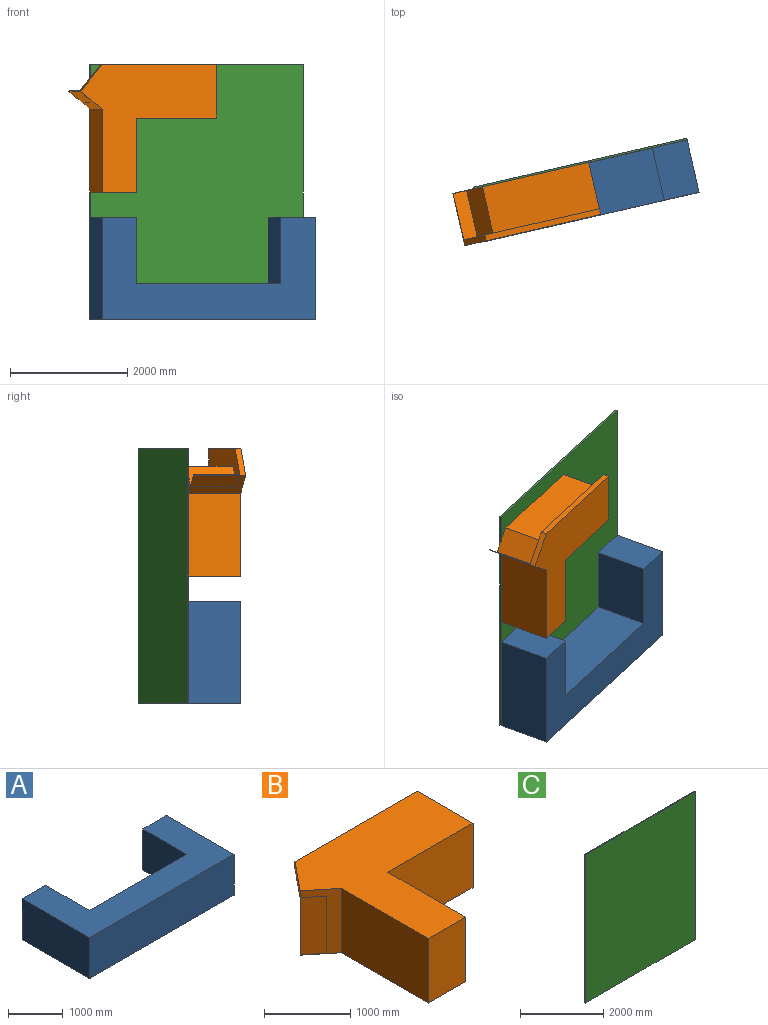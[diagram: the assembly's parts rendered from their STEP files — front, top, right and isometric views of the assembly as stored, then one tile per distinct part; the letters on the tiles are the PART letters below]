
ASSEMBLY  parts=3 mates=2
PART A: 10 faces, bbox 3733.8x1746.3x914.4 mm
  f0: plane 914.4x609.6mm, normal (0,1,0), area 557418.2mm2, adj f3,f5,f6,f7
  f1: plane 1746.25x914.4mm, normal (1,0,0), area 1596771mm2, adj f2,f4,f5,f6
  f2: plane 914.4x609.6mm, normal (0,1,0), area 557418.2mm2, adj f1,f5,f6,f9
  f3: plane 1746.25x914.4mm, normal (-1,0,0), area 1596771mm2, adj f0,f4,f5,f6
  f4: plane 3733.8x914.4mm, normal (0,-1,0), area 3414186.7mm2, adj f1,f3,f5,f6
  f5: plane 3733.8x1746.25mm, normal (0,0,1), area 3661928.2mm2, adj f0,f1,f2,f3,f4,f7,f8,f9
  f6: plane 3733.8x1746.25mm, normal (0,0,-1), area 3661928.2mm2, adj f0,f1,f2,f3,f4,f7,f8,f9
  f7: plane 1136.65x914.4mm, normal (1,0,0), area 1039352.8mm2, adj f0,f5,f6,f8
  f8: plane 2514.6x914.4mm, normal (0,1,0), area 2299350.2mm2, adj f5,f6,f7,f9
  f9: plane 1136.65x914.4mm, normal (-1,0,0), area 1039352.8mm2, adj f2,f5,f6,f8
PART B: 14 faces, bbox 2379.9x2190.2x914.4 mm
  f0: plane 2379.9x1885.4mm, normal (0,0,-1), area 2009196.6mm2, adj f1,f2,f4,f5,f6,f7,f8,f9
  f1: plane 1861.97x812.8mm, normal (0,1,0), area 1513411.7mm2, adj f0,f2,f11,f13
  f2: plane 914.4x914.4mm, normal (1,0,0), area 588385.9mm2, adj f0,f1,f3,f5,f10,f11
  f3: plane 2006.6x101.6mm, normal (0,1,0), area 203870.6mm2, adj f2,f6,f10,f11
  f4: plane 1275.8x914.4mm, normal (1,0,0), area 1166590.4mm2, adj f0,f5,f9,f10
  f5: plane 1397x914.4mm, normal (0,-1,0), area 1277416.8mm2, adj f0,f2,f4,f10
  f6: plane 914.4x457.2mm, normal (-0.77,0.63,0), area 64880.1mm2, adj f0,f3,f7,f10,f11,f12
  f7: plane 914.4x373.3mm, normal (-0.63,-0.77,0), area 440677.8mm2, adj f0,f6,f8,f10
  f8: plane 1428.2x914.4mm, normal (-1,0,0), area 1305945mm2, adj f0,f7,f9,f10
  f9: plane 914.4x609.6mm, normal (0,-1,0), area 557418.2mm2, adj f0,f4,f8,f10
  f10: plane 2379.9x2190.2mm, normal (0,0,1), area 2754790.2mm2, adj f2,f3,f4,f5,f6,f7,f8,f9
  f11: plane 2376.08x645.29mm, normal (0,0,-1), area 745593.5mm2, adj f1,f2,f3,f6,f12,f13
  f12: plane 812.8x236.1mm, normal (0.63,0.77,0), area 247741.4mm2, adj f0,f6,f11,f13
  f13: plane 812.8x340.49mm, normal (-0.77,0.63,0), area 357285mm2, adj f0,f1,f11,f12
PART C: 6 faces, bbox 3733.8x25.4x4356.1 mm
  f0: plane 4356.1x25.4mm, normal (1,0,0), area 110644.9mm2, adj f1,f3,f4,f5
  f1: plane 3733.8x25.4mm, normal (0,0,1), area 94838.5mm2, adj f0,f2,f4,f5
  f2: plane 4356.1x25.4mm, normal (-1,0,0), area 110644.9mm2, adj f1,f3,f4,f5
  f3: plane 3733.8x25.4mm, normal (0,0,-1), area 94838.5mm2, adj f0,f2,f4,f5
  f4: plane 4356.1x3733.8mm, normal (0,-1,0), area 16264806.2mm2, adj f0,f1,f2,f3
  f5: plane 4356.1x3733.8mm, normal (0,1,0), area 16264806.2mm2, adj f0,f1,f2,f3
PLACE A rot(axis=(0.99,0.11,0.11),90.7deg) t=(3711.23,757.56,-1950.23)mm
PLACE B rot(axis=(0.99,0.11,0.11),90.7deg) t=(2869.54,564.28,1075.54)mm
PLACE C rot(axis=(0,0,1),12.9deg) t=(3705.55,782.32,-645.31)mm
MATE fastened A.f6 <-> C.f4  axis (-0.22,0.97,0) through (5530.78,1175.38,-2823.36)mm
MATE planar C.f4 <-> B.f0  axis (0.22,-0.97,0) through (1891.69,339.74,1532.74)mm
